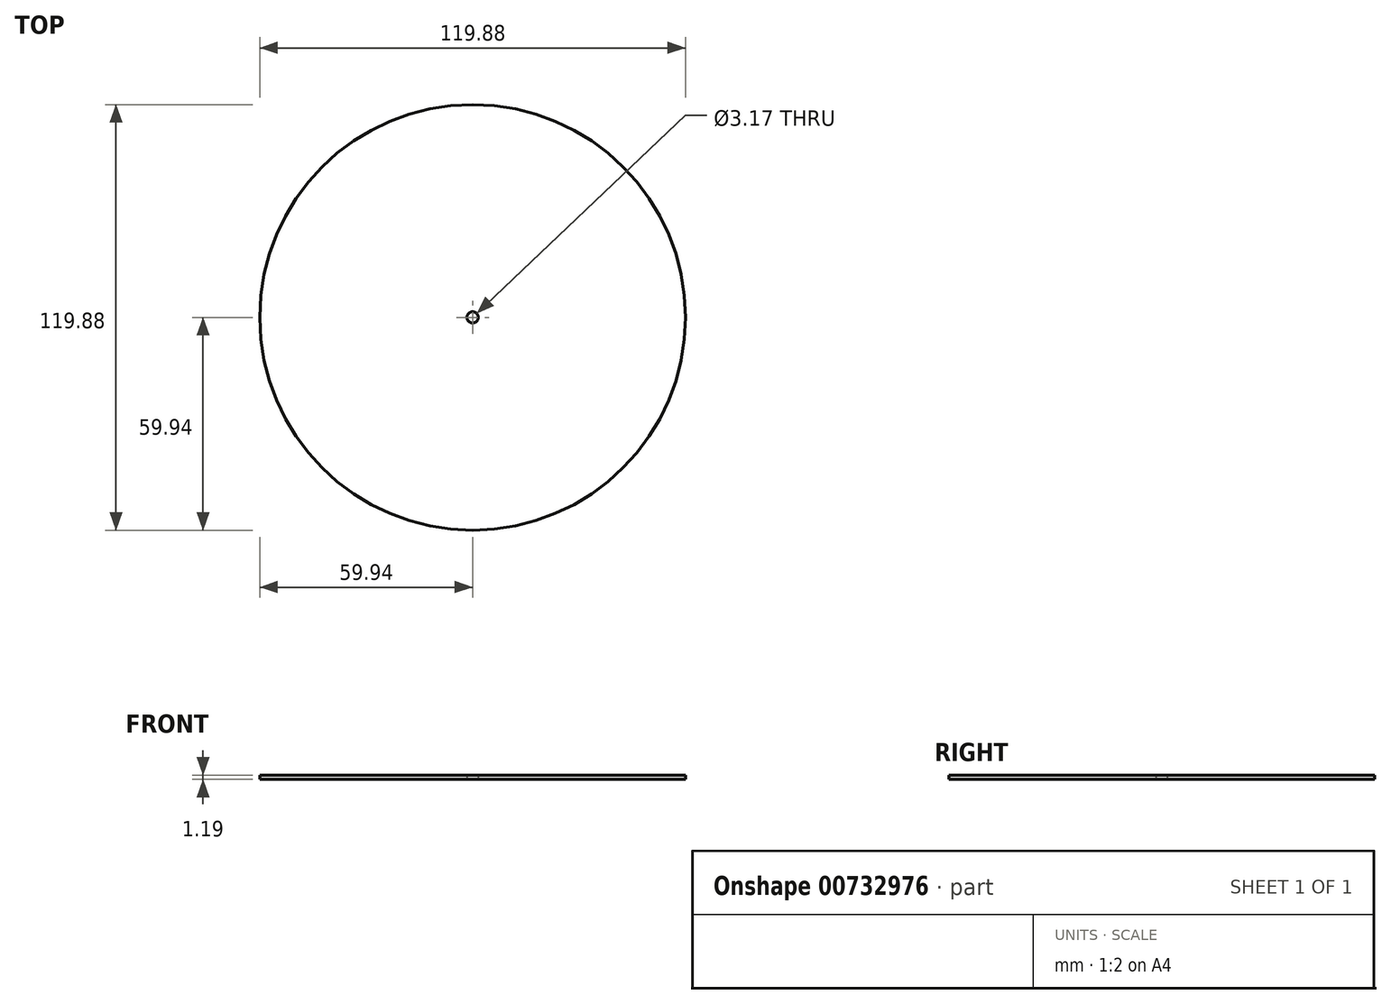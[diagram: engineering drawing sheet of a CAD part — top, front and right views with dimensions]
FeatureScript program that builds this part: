
annotation { "Feature Type Name" : "Feature", "Feature Type Description" : "" }
export const myFeature = defineFeature(function(context is Context, id is Id, definition is map)
    precondition{}
    {
        {
            var Q0;
            Q0=qCreatedBy(makeId("Top.planeOp"),FACE);
            var sketch = newSketch(context, id + "F0", { "sketchPlane" : qUnion([Q0])});
            skCircle(sketch, "E0", {"center": v(0, 0) * mm, "radius": 59.94 * mm});
            skCircle(sketch, "E1", {"center": v(0, 0) * mm, "radius": 1.59 * mm});
            skSolve(sketch);
        }
        {
            var Q0;
            Q0=makeQuery(id+"F0.imprint","IMPRINT",FACE,{"disambiguationData":[TD([[makeQuery(id+"F0.imprint","IMPRINT",EDGE,{"derivedFrom":sQuery(id+"F0.wireOp",EDGE,"E0")}),1.0]])]});
            extrude(context, id + "F1", {"entities" : qUnion([Q0]), "depth" : 1.2 * mm, "offsetDistance" : 25.4 * mm});
        }
    });
